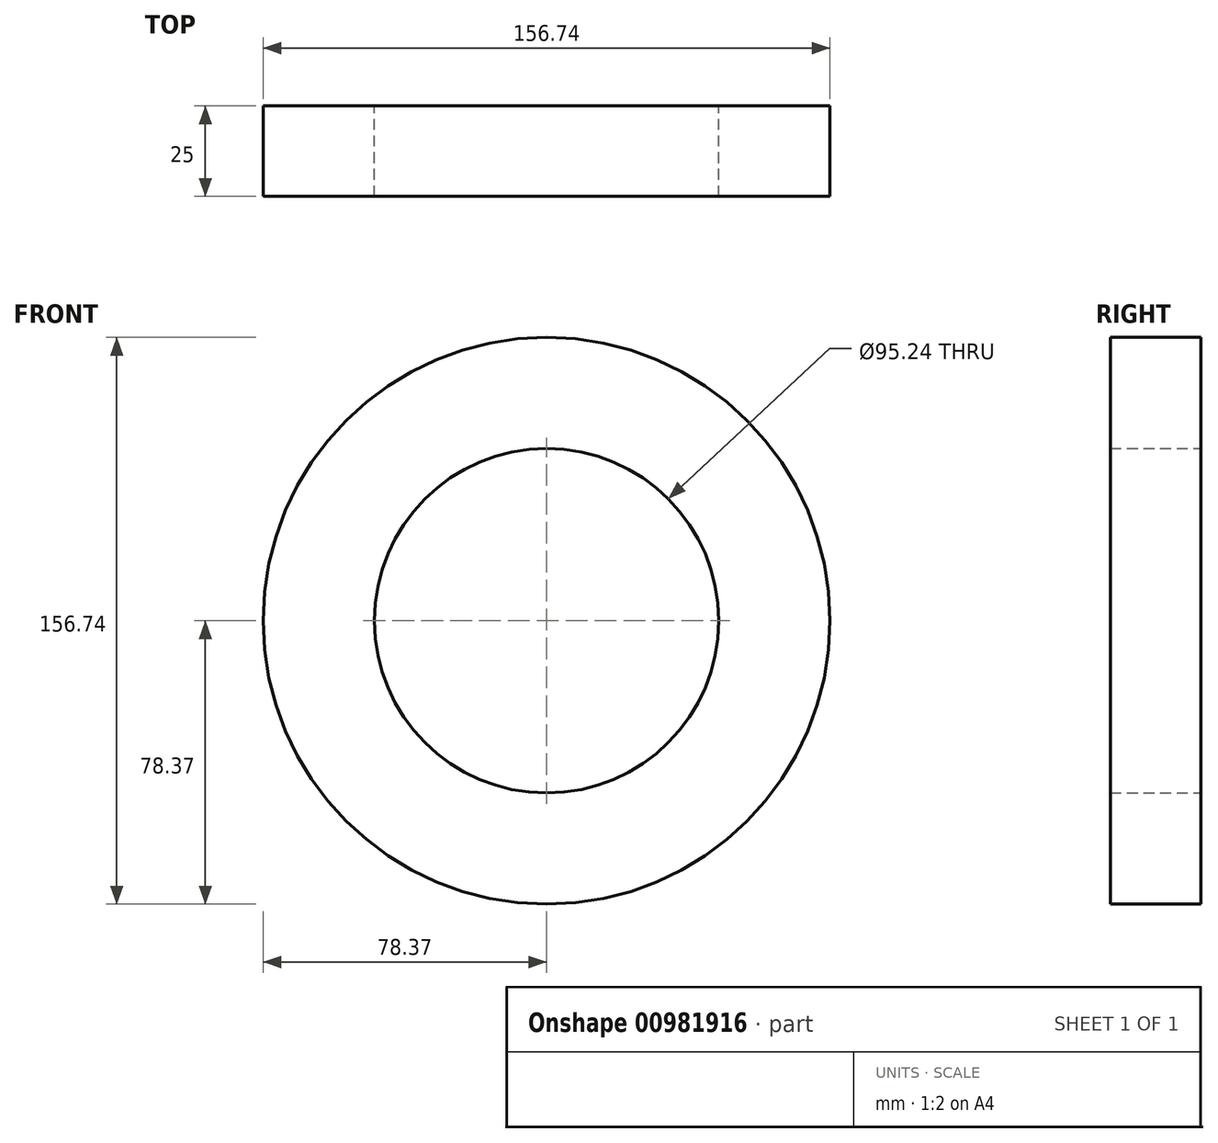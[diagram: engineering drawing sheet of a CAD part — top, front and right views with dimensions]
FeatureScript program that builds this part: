
annotation { "Feature Type Name" : "Feature", "Feature Type Description" : "" }
export const myFeature = defineFeature(function(context is Context, id is Id, definition is map)
    precondition{}
    {
        {
            var Q0;
            Q0=qCreatedBy(makeId("Front.planeOp"),FACE);
            var sketch = newSketch(context, id + "F0", { "sketchPlane" : qUnion([Q0])});
            skCircle(sketch, "E0", {"center": v(0, 0) * mm, "radius": 78.37 * mm});
            skCircle(sketch, "E1", {"center": v(0, 0) * mm, "radius": 47.62 * mm});
            skSolve(sketch);
        }
        {
            var Q0;
            Q0=makeQuery(id+"F0.imprint","IMPRINT",FACE,{"disambiguationData":[TD([[makeQuery(id+"F0.imprint","IMPRINT",EDGE,{"derivedFrom":sQuery(id+"F0.wireOp",EDGE,"E0")}),1.0]])]});
            extrude(context, id + "F1", {"entities" : qUnion([Q0]), "depth" : 25 * mm, "offsetDistance" : 25 * mm});
        }
    });
